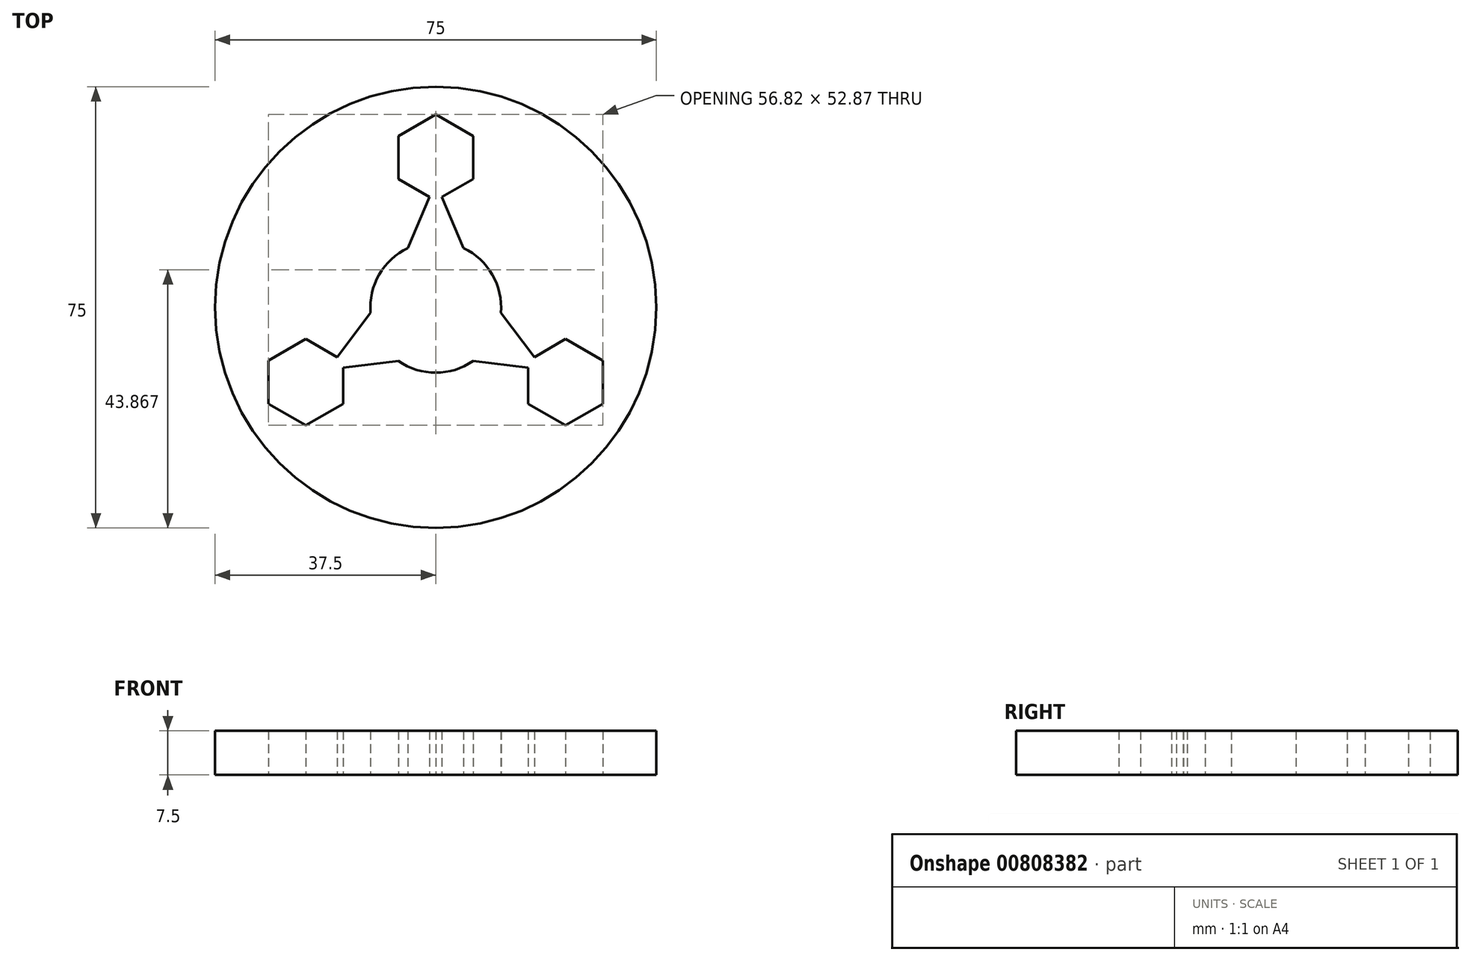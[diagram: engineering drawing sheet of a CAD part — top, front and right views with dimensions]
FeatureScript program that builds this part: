
annotation { "Feature Type Name" : "Feature", "Feature Type Description" : "" }
export const myFeature = defineFeature(function(context is Context, id is Id, definition is map)
    precondition{}
    {
        {
            var Q0;
            Q0=qCreatedBy(makeId("Top.planeOp"),FACE);
            var sketch = newSketch(context, id + "F0", { "sketchPlane" : qUnion([Q0])});
            skCircle(sketch, "E0", {"center": v(0, 0) * mm, "radius": 37.5 * mm});
            skArc(sketch, "E1", {"start": v(-4.72, 10.06) * mm, "mid": v(-9.62, 5.56) * mm, "end": v(-11.07, -0.94) * mm});
            skArc(sketch, "E2.trimOffspring", {"start": v(11.07, -0.94) * mm, "mid": v(9.62, 5.56) * mm, "end": v(4.72, 10.06) * mm});
            skArc(sketch, "E3.trimOffspring", {"start": v(-6.35, -9.12) * mm, "mid": v(0, -11.11) * mm, "end": v(6.35, -9.12) * mm});
            skLineSegment(sketch, "E4", {"start": v(0, -45.96) * mm, "end": v(5, -45.96) * mm});
            skLineSegment(sketch, "E5", {"start": v(5, -45.96) * mm, "end": v(4.06, -37.28) * mm});
            skLineSegment(sketch, "E6", {"start": v(0, -45.96) * mm, "end": v(-5, -45.96) * mm});
            skLineSegment(sketch, "E7.trimOffspring", {"start": v(-4.06, -37.28) * mm, "end": v(-5, -45.96) * mm});
            skLineSegment(sketch, "E8.trimOffspring", {"start": v(0, -37.5) * mm, "end": v(0, -45.96) * mm});
            skLineSegment(sketch, "E9", {"start": v(-4.72, 10.06) * mm, "end": v(0, 21.2) * mm});
            skLineSegment(sketch, "E10", {"start": v(0, 21.2) * mm, "end": v(4.72, 10.06) * mm});
            skLineSegment(sketch, "E11.1.0", {"start": v(-18.36, -10.6) * mm, "end": v(-11.07, -0.94) * mm});
            skLineSegment(sketch, "E11.1.1", {"start": v(-6.35, -9.12) * mm, "end": v(-18.36, -10.6) * mm});
            skLineSegment(sketch, "E11.2.0", {"start": v(18.36, -10.6) * mm, "end": v(6.35, -9.12) * mm});
            skLineSegment(sketch, "E11.2.1", {"start": v(11.07, -0.94) * mm, "end": v(18.36, -10.6) * mm});
            skCircle(sketch, "E12", {"center": v(0, 0) * mm, "radius": 31.37 * mm});
            skLineSegment(sketch, "E13", {"start": v(0, 21.2) * mm, "end": v(0, 25.47) * mm});
            skCircle(sketch, "E14.cCircle", {"center": v(0, 25.47) * mm, "radius": 6.35 * mm, "construction": true});
            skLineSegment(sketch, "E14.0", {"start": v(6.35, 29.14) * mm, "end": v(6.35, 21.8) * mm});
            skLineSegment(sketch, "E14.1", {"start": v(6.35, 21.8) * mm, "end": v(0, 18.14) * mm});
            skLineSegment(sketch, "E14.2", {"start": v(0, 18.14) * mm, "end": v(-6.35, 21.8) * mm});
            skLineSegment(sketch, "E14.3", {"start": v(-6.35, 21.8) * mm, "end": v(-6.35, 29.14) * mm});
            skLineSegment(sketch, "E14.4", {"start": v(-6.35, 29.14) * mm, "end": v(0, 32.8) * mm});
            skLineSegment(sketch, "E14.5", {"start": v(0, 32.8) * mm, "end": v(6.35, 29.14) * mm});
            skPoint(sketch, "E14.0.midPoint", {"position": v(6.35, 25.47) * mm});
            skLineSegment(sketch, "E15.1.0", {"start": v(-28.4, -16.4) * mm, "end": v(-28.4, -9.07) * mm});
            skLineSegment(sketch, "E15.1.1", {"start": v(-22.06, -20.07) * mm, "end": v(-28.4, -16.4) * mm});
            skLineSegment(sketch, "E15.1.2", {"start": v(-15.7, -16.4) * mm, "end": v(-22.06, -20.07) * mm});
            skLineSegment(sketch, "E15.1.3", {"start": v(-28.4, -9.07) * mm, "end": v(-22.06, -5.4) * mm});
            skCircle(sketch, "E15.1.4", {"center": v(-22.06, -12.74) * mm, "radius": 6.35 * mm, "construction": true});
            skLineSegment(sketch, "E15.1.5", {"start": v(-22.06, -5.4) * mm, "end": v(-15.7, -9.07) * mm});
            skLineSegment(sketch, "E15.1.6", {"start": v(-15.7, -9.07) * mm, "end": v(-15.7, -16.4) * mm});
            skLineSegment(sketch, "E15.2.0", {"start": v(28.4, -16.4) * mm, "end": v(22.06, -20.07) * mm});
            skLineSegment(sketch, "E15.2.1", {"start": v(28.4, -9.07) * mm, "end": v(28.4, -16.4) * mm});
            skLineSegment(sketch, "E15.2.2", {"start": v(22.06, -5.4) * mm, "end": v(28.4, -9.07) * mm});
            skLineSegment(sketch, "E15.2.3", {"start": v(22.06, -20.07) * mm, "end": v(15.7, -16.4) * mm});
            skCircle(sketch, "E15.2.4", {"center": v(22.06, -12.74) * mm, "radius": 6.35 * mm, "construction": true});
            skLineSegment(sketch, "E15.2.5", {"start": v(15.7, -16.4) * mm, "end": v(15.7, -9.07) * mm});
            skLineSegment(sketch, "E15.2.6", {"start": v(15.7, -9.07) * mm, "end": v(22.06, -5.4) * mm});
            skSolve(sketch);
        }
        {
            var Q0;
            {var subQ7=sQuery(id+"F0.wireOp",EDGE,"E1");Q0=makeQuery(id+"F0.imprint","IMPRINT",FACE,{"disambiguationData":[TD([[makeQuery(id+"F0.imprint","IMPRINT",EDGE,{"derivedFrom":subQ7}),-1.0]])]});}
            var Q1;
            {var subQ6=sQuery(id+"F0.wireOp",EDGE,"E2.trimOffspring");Q1=makeQuery(id+"F0.imprint","IMPRINT",FACE,{"disambiguationData":[TD([[makeQuery(id+"F0.imprint","IMPRINT",EDGE,{"derivedFrom":subQ6}),-1.0]])]});}
            var Q2;
            {var subQ16=sQuery(id+"F0.wireOp",EDGE,"E0");var subQ17=makeQuery(id+"F0.imprint","INTERSECT",VERTEX,{"derivedFrom":[subQ16,sQuery(id+"F0.wireOp",EDGE,"E7.trimOffspring")]});Q2=makeQuery(id+"F0.imprint","IMPRINT",FACE,{"disambiguationData":[TD([[makeQuery(id+"F0.imprint","IMPRINT",EDGE,{"disambiguationData":[TD([[subQ17,-1.0]])],"derivedFrom":subQ16}),1.0]])]});}
            var Q3;
            {var subQ9=sQuery(id+"F0.wireOp",EDGE,"E3.trimOffspring");Q3=makeQuery(id+"F0.imprint","IMPRINT",FACE,{"disambiguationData":[TD([[makeQuery(id+"F0.imprint","IMPRINT",EDGE,{"derivedFrom":subQ9}),-1.0]])]});}
            extrude(context, id + "F1", {"entities" : qUnion([Q0, Q1, Q2, Q3]), "depth" : 7.5 * mm, "offsetDistance" : 25 * mm});
        }
    });
